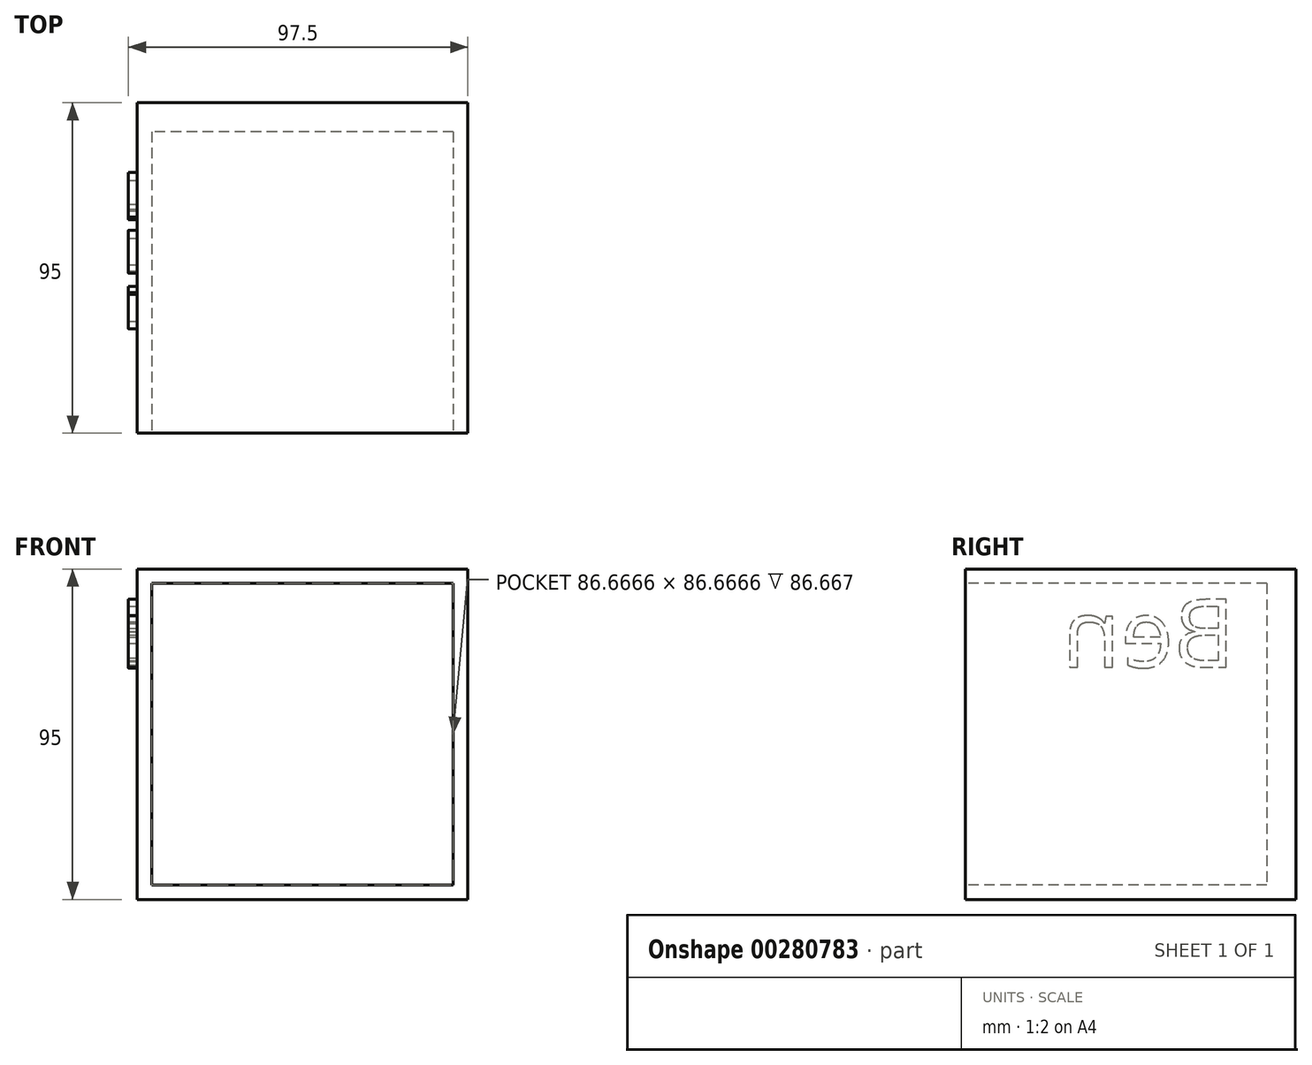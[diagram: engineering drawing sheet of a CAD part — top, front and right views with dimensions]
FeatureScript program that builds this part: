
annotation { "Feature Type Name" : "Feature", "Feature Type Description" : "" }
export const myFeature = defineFeature(function(context is Context, id is Id, definition is map)
    precondition{}
    {
        {
            var Q0;
            Q0=qCreatedBy(makeId("Front.planeOp"),FACE);
            var sketch = newSketch(context, id + "F0", { "sketchPlane" : qUnion([Q0])});
            skLineSegment(sketch, "E0.bottom", {"start": v(47.5, 47.5) * mm, "end": v(-47.5, 47.5) * mm});
            skLineSegment(sketch, "E0.top", {"start": v(47.5, -47.5) * mm, "end": v(-47.5, -47.5) * mm});
            skLineSegment(sketch, "E0.left", {"start": v(47.5, 47.5) * mm, "end": v(47.5, -47.5) * mm});
            skLineSegment(sketch, "E0.right", {"start": v(-47.5, 47.5) * mm, "end": v(-47.5, -47.5) * mm});
            skPoint(sketch, "E0.middle", {"position": v(0, 0) * mm});
            skSolve(sketch);
        }
        {
            var Q0;
            Q0=makeQuery(id+"F0.imprint","IMPRINT",FACE,{"disambiguationData":[TD([[makeQuery(id+"F0.imprint","IMPRINT",EDGE,{"derivedFrom":sQuery(id+"F0.wireOp",EDGE,"E0.bottom")}),1.0]])]});
            extrude(context, id + "F1", {"entities" : qUnion([Q0]), "depth" : 95 * mm});
        }
        {
            var Q0;
            Q0=makeQuery(id+"F1.opExtrude","CAP_FACE",FACE,{"disambiguationData":[OSD([sQuery(id+"F0.wireOp",EDGE,"E0.bottom"),sQuery(id+"F0.wireOp",EDGE,"E0.top"),sQuery(id+"F0.wireOp",EDGE,"E0.left"),sQuery(id+"F0.wireOp",EDGE,"E0.right")])],"isStart":false});
            var sketch = newSketch(context, id + "F2", { "sketchPlane" : qUnion([Q0])});
            skLineSegment(sketch, "E1.bottom", {"start": v(43.33, 43.33) * mm, "end": v(-43.33, 43.33) * mm});
            skLineSegment(sketch, "E1.top", {"start": v(43.33, -43.33) * mm, "end": v(-43.33, -43.33) * mm});
            skLineSegment(sketch, "E1.left", {"start": v(43.33, 43.33) * mm, "end": v(43.33, -43.33) * mm});
            skLineSegment(sketch, "E1.right", {"start": v(-43.33, 43.33) * mm, "end": v(-43.33, -43.33) * mm});
            skPoint(sketch, "E1.middle", {"position": v(0, 0) * mm});
            skSolve(sketch);
        }
        {
            var Q0;
            Q0=makeQuery(id+"F2.imprint","IMPRINT",FACE,{"disambiguationData":[TD([[makeQuery(id+"F2.imprint","IMPRINT",EDGE,{"derivedFrom":sQuery(id+"F2.wireOp",EDGE,"E1.bottom")}),1.0]])]});
            extrude(context, id + "F3", {"entities" : qUnion([Q0]), "operationType" : NewBodyOperationType.REMOVE, "oppositeDirection" : true, "depth" : 86.67 * mm});
        }
        {
            var Q0;
            Q0=makeQuery(id+"F1.opExtrude","SWEPT_FACE",FACE,{"disambiguationData":[OSD([sQuery(id+"F0.wireOp",EDGE,"E0.right")])]});
            var sketch = newSketch(context, id + "F4", { "sketchPlane" : qUnion([Q0])});
            skText(sketch, "E2", { "text": "Ben", "fontName": "OpenSans-Regular.ttf"});
            const initialGuessF4  = {"E2": [0.01732, 0.01922, 1, 0, 0.0197]};
            skSetInitialGuess(sketch, initialGuessF4);
            skSolve(sketch);
        }
        {
            var Q0;
            Q0 = qSketchRegion(id + "F4", true);
            extrude(context, id + "F5", {"entities" : qUnion([Q0]), "operationType" : NewBodyOperationType.ADD, "depth" : 2.5 * mm});
        }
    });
